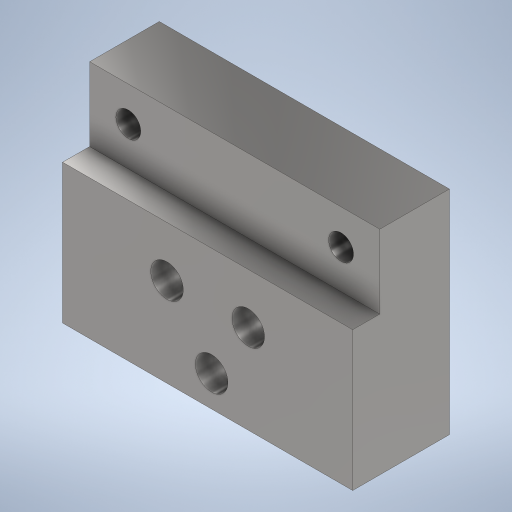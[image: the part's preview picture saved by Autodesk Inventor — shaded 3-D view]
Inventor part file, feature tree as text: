
AUTODESK INVENTOR PART (.ipt)
format: ipt  version: 2023.2 (Build 272271000, 271)  size: 261,632 bytes
history: native  units: mm
features: sketch x3, hole x2, extrude x1
ambient origin geometry x8: Origin, YZ Plane, XZ Plane, XY Plane, X Axis, Y Axis, Z Axis, Center Point
bodies: Solid1 (feature_tree)
feature tree (6):
  extrude  "Extrusion1"  Depth=18.0mm
  hole  "Hole1"  [1 undecoded]
  hole  "Hole2"  [1 undecoded]
  sketch  "Sketch1"  dims[d0=55.0mm d1=18.0mm]
  sketch  "Sketch2"  dims[d2=19.0mm d3=7.0mm]
  sketch  "Sketch3"  dims[d4=36.0mm d5=75.0mm d6=0.0mm d7=8.0mm d8=8.4mm d9=12.0mm d10=15.0mm d11=10.0mm d12=90.0deg d13=20.0mm d14=20.594885mm d15=23.0mm d16=23.0mm d17=10.0mm d18=10.0mm d19=6.4mm d20=6.0mm d21=11.0mm d22=7.0mm d23=90.0deg d24=8.0mm d25=20.594885mm d26=36.461809mm d27=27.0mm d28=27.0mm d29=46.0mm d30=46.0mm]
note: 2 required parameter values undecoded (feature->parameter linkage not recoverable at this tier; creation-order binding heuristic only, values carry confidence <= 0.55)
